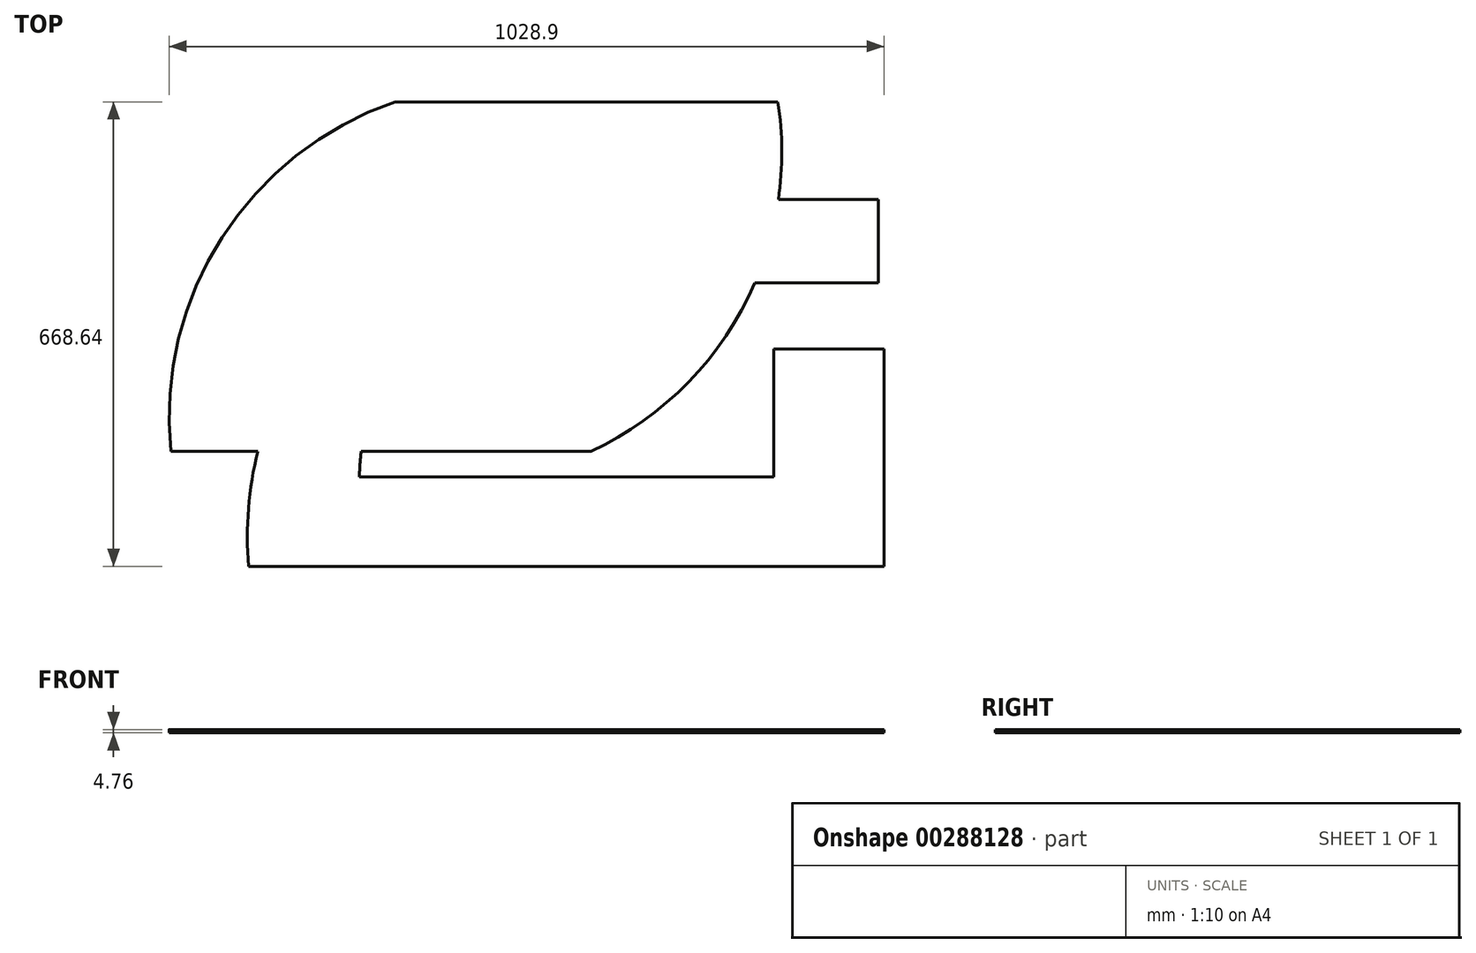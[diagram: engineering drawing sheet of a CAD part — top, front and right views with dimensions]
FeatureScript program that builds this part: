
annotation { "Feature Type Name" : "Feature", "Feature Type Description" : "" }
export const myFeature = defineFeature(function(context is Context, id is Id, definition is map)
    precondition{}
    {
        {
            var Q0;
            Q0=qCreatedBy(makeId("Top.planeOp"),FACE);
            var sketch = newSketch(context, id + "F0", { "sketchPlane" : qUnion([Q0])});
            skLineSegment(sketch, "E0", {"start": v(59.28, -3.6) * mm, "end": v(85.74, -3.6) * mm});
            skLineSegment(sketch, "E1", {"start": v(85.74, -3.6) * mm, "end": v(85.74, -55.72) * mm});
            skLineSegment(sketch, "E2", {"start": v(85.74, -55.72) * mm, "end": v(-66.66, -55.72) * mm});
            skLineSegment(sketch, "E3", {"start": v(59.28, -3.6) * mm, "end": v(59.28, -34.24) * mm});
            skLineSegment(sketch, "E4", {"start": v(59.28, -34.24) * mm, "end": v(-40.08, -34.24) * mm});
            skArc(sketch, "E5", {"start": v(1.07, 12.25) * mm, "mid": v(-28.27, -3.23) * mm, "end": v(-40.08, -34.24) * mm});
            skLineSegment(sketch, "E6", {"start": v(1.07, 12.25) * mm, "end": v(27.63, 12.25) * mm});
            skLineSegment(sketch, "E7", {"start": v(54.72, 12.25) * mm, "end": v(84.36, 12.25) * mm});
            skLineSegment(sketch, "E8", {"start": v(84.36, 12.25) * mm, "end": v(84.36, 32.26) * mm});
            skLineSegment(sketch, "E9", {"start": v(84.36, 32.26) * mm, "end": v(60.38, 32.26) * mm});
            skLineSegment(sketch, "E10", {"start": v(34.08, 32.26) * mm, "end": v(-7.06, 32.26) * mm});
            skArc(sketch, "E11", {"start": v(-7.06, 32.26) * mm, "mid": v(-52.43, -1.18) * mm, "end": v(-66.66, -55.72) * mm});
            skArc(sketch, "E12", {"start": v(-31.48, 55.72) * mm, "mid": v(-73.04, 23.2) * mm, "end": v(-85.34, -28.12) * mm});
            skLineSegment(sketch, "E13", {"start": v(-31.48, 55.72) * mm, "end": v(60.26, 55.72) * mm});
            skArc(sketch, "E14", {"start": v(15.49, -28.12) * mm, "mid": v(51.86, 6.33) * mm, "end": v(60.26, 55.72) * mm});
            skLineSegment(sketch, "E15", {"start": v(15.49, -28.12) * mm, "end": v(-39.66, -28.12) * mm});
            skLineSegment(sketch, "E16", {"start": v(-64.46, -28.12) * mm, "end": v(-85.34, -28.12) * mm});
            skArc(sketch, "E17", {"start": v(-21.3, 37.21) * mm, "mid": v(-48.63, 20.43) * mm, "end": v(-61.9, -8.75) * mm});
            skLineSegment(sketch, "E18", {"start": v(-21.3, 37.21) * mm, "end": v(34.24, 37.63) * mm});
            skArc(sketch, "E19", {"start": v(0.74, -8.75) * mm, "mid": v(25.34, 8.77) * mm, "end": v(34.24, 37.63) * mm});
            skLineSegment(sketch, "E20", {"start": v(0.74, -8.75) * mm, "end": v(-32.47, -8.75) * mm});
            skLineSegment(sketch, "E21", {"start": v(-57, -8.75) * mm, "end": v(-61.9, -8.75) * mm});
            skSolve(sketch);
        }
        {
            var Q0;
            Q0 = qSketchRegion(id + "F0", true);
            extrude(context, id + "F1", {"entities" : qUnion([Q0]), "depth" : 0.8 * mm});
        }
        {
            var Q0;
            Q0=makeQuery(id+"F1.opExtrude","SWEPT_BODY",BODY,{"disambiguationData":[OSD([sQuery(id+"F0.wireOp",EDGE,"E0"),sQuery(id+"F0.wireOp",EDGE,"E1"),sQuery(id+"F0.wireOp",EDGE,"E2"),sQuery(id+"F0.wireOp",EDGE,"E3"),sQuery(id+"F0.wireOp",EDGE,"E4"),sQuery(id+"F0.wireOp",EDGE,"E5"),sQuery(id+"F0.wireOp",EDGE,"E6"),sQuery(id+"F0.wireOp",EDGE,"E7"),sQuery(id+"F0.wireOp",EDGE,"E8"),sQuery(id+"F0.wireOp",EDGE,"E9"),sQuery(id+"F0.wireOp",EDGE,"E10"),sQuery(id+"F0.wireOp",EDGE,"E11"),sQuery(id+"F0.wireOp",EDGE,"E12"),sQuery(id+"F0.wireOp",EDGE,"E13"),sQuery(id+"F0.wireOp",EDGE,"E14"),sQuery(id+"F0.wireOp",EDGE,"E15"),sQuery(id+"F0.wireOp",EDGE,"E16"),sQuery(id+"F0.wireOp",EDGE,"E17"),sQuery(id+"F0.wireOp",EDGE,"E18"),sQuery(id+"F0.wireOp",EDGE,"E19"),sQuery(id+"F0.wireOp",EDGE,"E20"),sQuery(id+"F0.wireOp",EDGE,"E21")])]});
            var Q1;
            Q1=qCreatedBy(makeId("Origin.pointOp"),VERTEX);
            transform(context, id + "F2", {"entities" : qUnion([Q0]), "transformType" : TransformType.SCALE_UNIFORMLY, "scale" : 6, "scalePoint" : qUnion([Q1]), "makeCopy" : false});
        }
    });
